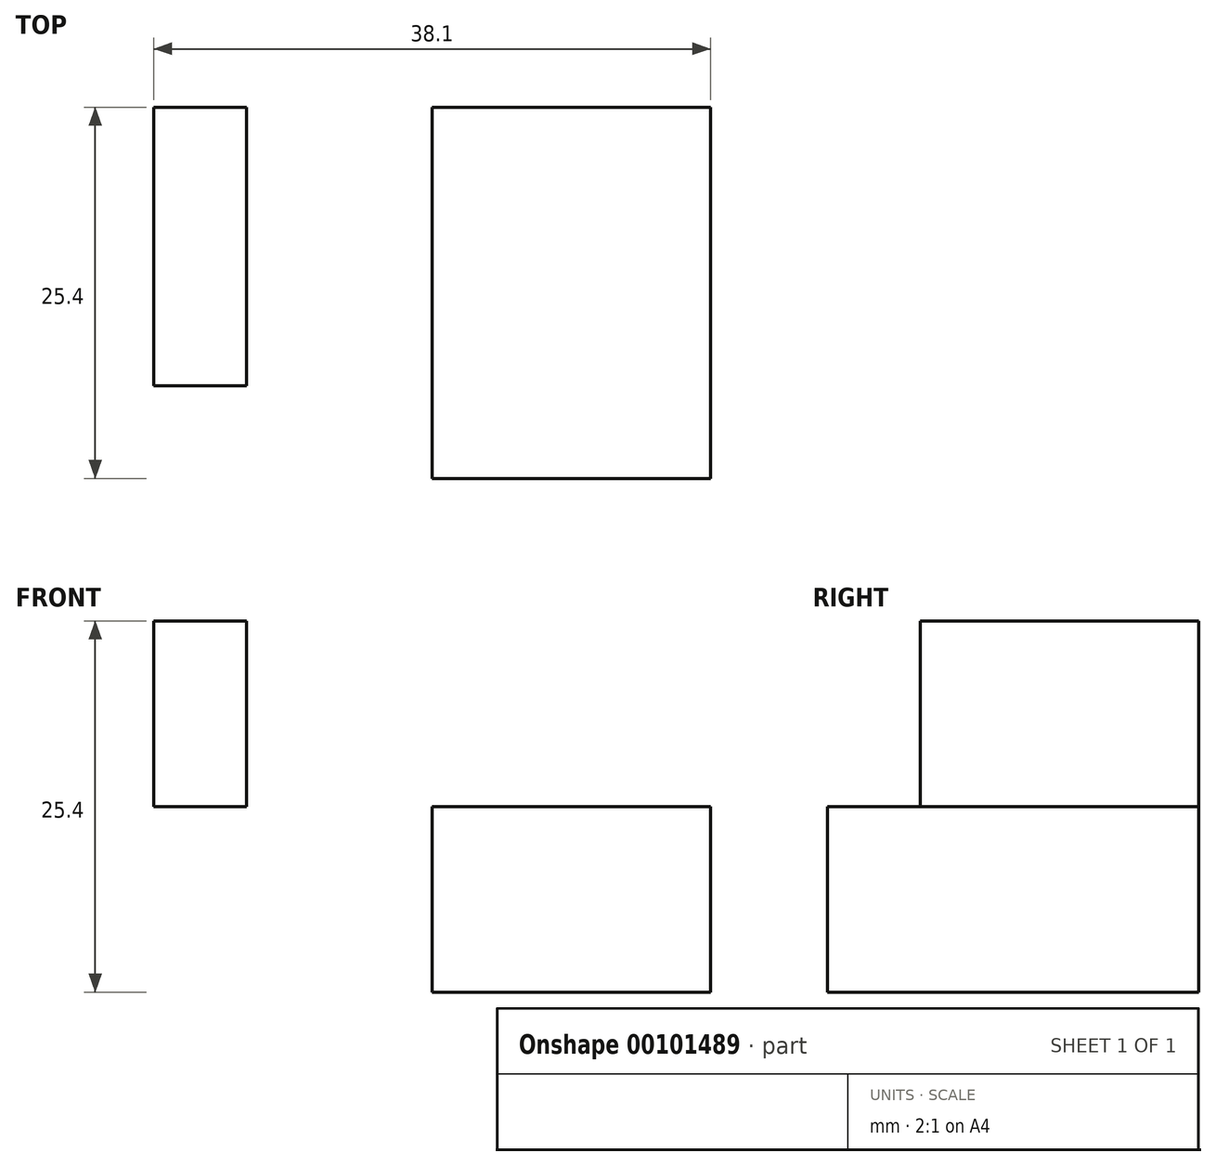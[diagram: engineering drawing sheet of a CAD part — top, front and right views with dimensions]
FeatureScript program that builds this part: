
annotation { "Feature Type Name" : "Feature", "Feature Type Description" : "" }
export const myFeature = defineFeature(function(context is Context, id is Id, definition is map)
    precondition{}
    {
        {
            var Q0;
            Q0=qCreatedBy(makeId("Front.planeOp"),FACE);
            var sketch = newSketch(context, id + "F0", { "sketchPlane" : qUnion([Q0])});
            skLineSegment(sketch, "E0", {"start": v(38.1, 0) * mm, "end": v(38.1, 12.7) * mm});
            skLineSegment(sketch, "E1", {"start": v(38.1, 12.7) * mm, "end": v(6.35, 12.7) * mm});
            skLineSegment(sketch, "E2", {"start": v(6.35, 12.7) * mm, "end": v(6.35, 25.4) * mm});
            skLineSegment(sketch, "E3", {"start": v(6.35, 25.4) * mm, "end": v(0, 25.4) * mm});
            skLineSegment(sketch, "E4", {"start": v(0, 25.4) * mm, "end": v(0, 0) * mm});
            skLineSegment(sketch, "E5", {"start": v(0, 0) * mm, "end": v(38.1, 0) * mm});
            skLineSegment(sketch, "E6", {"start": v(38.1, 0) * mm, "end": v(19.05, 0) * mm});
            skLineSegment(sketch, "E7", {"start": v(19.05, 0) * mm, "end": v(19.05, 12.7) * mm});
            skLineSegment(sketch, "E8", {"start": v(6.35, 12.7) * mm, "end": v(0, 12.7) * mm});
            skSolve(sketch);
        }
        {
            var Q0;
            {var subQ0=sQuery(id+"F0.wireOp",EDGE,"E0");Q0=makeQuery(id+"F0.imprint","IMPRINT",FACE,{"disambiguationData":[TD([[makeQuery(id+"F0.imprint","IMPRINT",EDGE,{"derivedFrom":subQ0}),1.0]])]});}
            var Q1;
            {var subQ3=sQuery(id+"F0.wireOp",EDGE,"E5");Q1=makeQuery(id+"F0.imprint","IMPRINT",FACE,{"disambiguationData":[TD([[makeQuery(id+"F0.imprint","IMPRINT",EDGE,{"derivedFrom":subQ3}),1.0]])]});}
            extrude(context, id + "F1", {"entities" : qUnion([Q0, Q1]), "depth" : 12.7 * mm});
        }
        {
            var Q0;
            Q0=makeQuery(id+"F0.imprint","IMPRINT",FACE,{"disambiguationData":[TD([[makeQuery(id+"F0.imprint","IMPRINT",EDGE,{"derivedFrom":sQuery(id+"F0.wireOp",EDGE,"E2")}),1.0]])]});
            extrude(context, id + "F2", {"entities" : qUnion([Q0]), "operationType" : NewBodyOperationType.ADD, "depth" : 19.05 * mm});
        }
        {
            var Q0;
            {var subQ3=sQuery(id+"F0.wireOp",EDGE,"E5");Q0=makeQuery(id+"F0.imprint","IMPRINT",FACE,{"disambiguationData":[TD([[makeQuery(id+"F0.imprint","IMPRINT",EDGE,{"derivedFrom":subQ3}),1.0]])]});}
            extrude(context, id + "F3", {"entities" : qUnion([Q0]), "operationType" : NewBodyOperationType.ADD, "depth" : 25.4 * mm});
        }
    });
